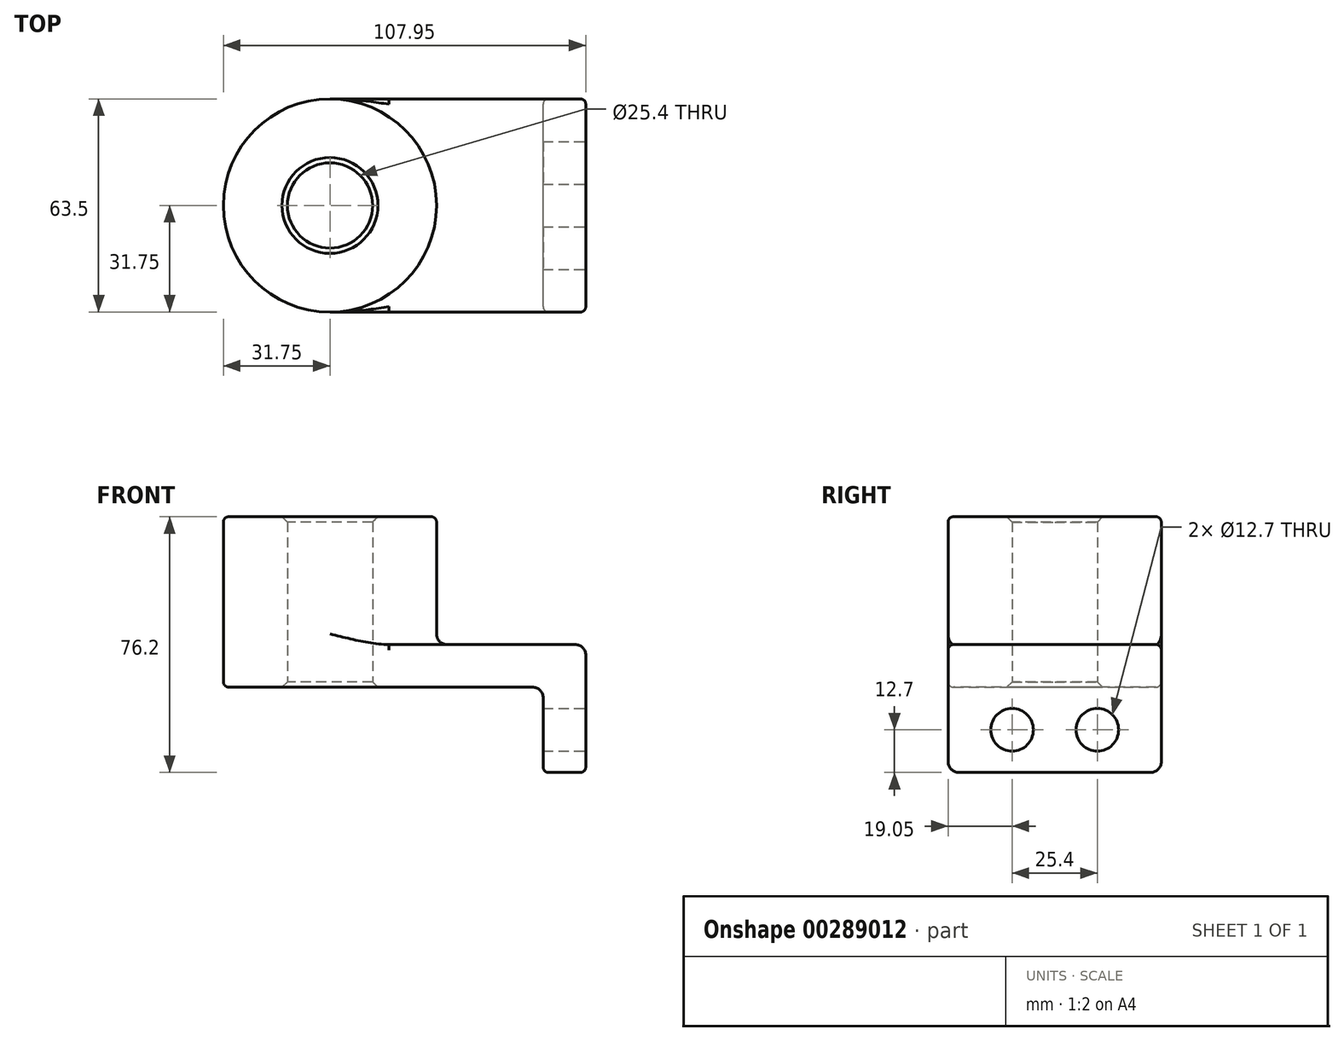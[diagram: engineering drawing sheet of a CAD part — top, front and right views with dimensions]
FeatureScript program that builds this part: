
annotation { "Feature Type Name" : "Feature", "Feature Type Description" : "" }
export const myFeature = defineFeature(function(context is Context, id is Id, definition is map)
    precondition{}
    {
        {
            var Q0;
            Q0=qCreatedBy(makeId("Top.planeOp"),FACE);
            var sketch = newSketch(context, id + "F0", { "sketchPlane" : qUnion([Q0])});
            skLineSegment(sketch, "E0.rect.bottom", {"start": v(-38.1, -31.75) * mm, "end": v(38.1, -31.75) * mm});
            skLineSegment(sketch, "E0.rect.top", {"start": v(-38.1, 31.75) * mm, "end": v(38.1, 31.75) * mm});
            skLineSegment(sketch, "E0.rect.left", {"start": v(-38.1, -31.75) * mm, "end": v(-38.1, 31.75) * mm});
            skLineSegment(sketch, "E0.rect.right", {"start": v(38.1, -31.75) * mm, "end": v(38.1, 31.75) * mm});
            skPoint(sketch, "E0.rect.middle", {"position": v(0, 0) * mm});
            skCircle(sketch, "E1", {"center": v(-38.1, 0) * mm, "radius": 31.75 * mm});
            skCircle(sketch, "E2", {"center": v(-38.1, 0) * mm, "radius": 12.7 * mm});
            skSolve(sketch);
        }
        {
            var Q0;
            {var subQ2=sQuery(id+"F0.wireOp",EDGE,"E0.rect.left");var subQ4=sQuery(id+"F0.wireOp",EDGE,"E0.rect.bottom");var subQ7=sQuery(id+"F0.wireOp",EDGE,"E2");var subQ9=makeQuery(id+"F0.imprint","INTERSECT",VERTEX,{"disambiguationData":[OD(0.0)],"derivedFrom":[subQ2,subQ7]});Q0=qUnion([makeQuery(id+"F0.imprint","IMPRINT",FACE,{"disambiguationData":[TD([[makeQuery(id+"F0.imprint","IMPRINT",EDGE,{"derivedFrom":subQ4}),1.0]])]}),makeQuery(id+"F0.imprint","IMPRINT",FACE,{"disambiguationData":[TD([[makeQuery(id+"F0.imprint","IMPRINT",EDGE,{"disambiguationData":[TD([[subQ9,1.0]])],"derivedFrom":subQ7}),-1.0]])]}),makeQuery(id+"F0.imprint","IMPRINT",FACE,{"disambiguationData":[TD([[makeQuery(id+"F0.imprint","IMPRINT",EDGE,{"disambiguationData":[TD([[subQ9,-1.0]])],"derivedFrom":subQ7}),-1.0]])]})]);}
            extrude(context, id + "F1", {"entities" : qUnion([Q0]), "depth" : 12.7 * mm});
        }
        {
            var Q0;
            {var subQ0=sQuery(id+"F0.wireOp",EDGE,"E2");var subQ1=sQuery(id+"F0.wireOp",EDGE,"E0.rect.left");var subQ3=makeQuery(id+"F0.imprint","INTERSECT",VERTEX,{"disambiguationData":[OD(0.0)],"derivedFrom":[subQ1,subQ0]});Q0=makeQuery(id+"F0.imprint","IMPRINT",FACE,{"disambiguationData":[TD([[makeQuery(id+"F0.imprint","IMPRINT",EDGE,{"disambiguationData":[TD([[subQ3,1.0]])],"derivedFrom":subQ0}),-1.0]])]});}
            var Q1;
            {var subQ0=sQuery(id+"F0.wireOp",EDGE,"E2");var subQ1=sQuery(id+"F0.wireOp",EDGE,"E0.rect.left");var subQ3=makeQuery(id+"F0.imprint","INTERSECT",VERTEX,{"disambiguationData":[OD(0.0)],"derivedFrom":[subQ1,subQ0]});Q1=makeQuery(id+"F0.imprint","IMPRINT",FACE,{"disambiguationData":[TD([[makeQuery(id+"F0.imprint","IMPRINT",EDGE,{"disambiguationData":[TD([[subQ3,-1.0]])],"derivedFrom":subQ0}),-1.0]])]});}
            extrude(context, id + "F2", {"entities" : qUnion([Q0, Q1]), "operationType" : NewBodyOperationType.ADD, "depth" : 50.8 * mm});
        }
        {
            var Q0;
            Q0=makeQuery(id+"F1.opExtrude","SWEPT_FACE",FACE,{"disambiguationData":[OSD([sQuery(id+"F0.wireOp",EDGE,"E0.rect.right")])]});
            var sketch = newSketch(context, id + "F3", { "sketchPlane" : qUnion([Q0])});
            skLineSegment(sketch, "E3.bottom", {"start": v(-31.75, 12.7) * mm, "end": v(31.75, 12.7) * mm});
            skLineSegment(sketch, "E3.top", {"start": v(-31.75, -25.4) * mm, "end": v(31.75, -25.4) * mm});
            skLineSegment(sketch, "E3.left", {"start": v(-31.75, 12.7) * mm, "end": v(-31.75, -25.4) * mm});
            skLineSegment(sketch, "E3.right", {"start": v(31.75, 12.7) * mm, "end": v(31.75, -25.4) * mm});
            skLineSegment(sketch, "E4", {"start": v(0, 0) * mm, "end": v(0, -25.4) * mm, "construction": true});
            skCircle(sketch, "E5", {"center": v(-12.7, -12.7) * mm, "radius": 6.35 * mm});
            skCircle(sketch, "E6.0.MirrorC", {"center": v(12.7, -12.7) * mm, "radius": 6.35 * mm});
            skSolve(sketch);
        }
        {
            var Q0;
            {var subQ3=sQuery(id+"F3.wireOp",EDGE,"E3.bottom");var subQ7=sQuery(id+"F3.wireOp",EDGE,"E3.top");Q0=qUnion([makeQuery(id+"F3.imprint","IMPRINT",FACE,{"disambiguationData":[TD([[makeQuery(id+"F3.imprint","IMPRINT",EDGE,{"derivedFrom":subQ3}),-1.0]])]}),makeQuery(id+"F3.imprint","IMPRINT",FACE,{"disambiguationData":[TD([[makeQuery(id+"F3.imprint","IMPRINT",EDGE,{"derivedFrom":subQ7}),1.0]])]})]);}
            extrude(context, id + "F4", {"entities" : qUnion([Q0]), "operationType" : NewBodyOperationType.ADD, "oppositeDirection" : true, "depth" : 12.7 * mm});
        }
        {
            var Q0;
            {var subQ0=sQuery(id+"F0.wireOp",EDGE,"E1");Q0=makeQuery(id+"F2.boolean.opBoolean","INTERSECT",EDGE,{"derivedFrom":[makeQuery(id+"F1.opExtrude","CAP_FACE",FACE,{"disambiguationData":[OSD([sQuery(id+"F0.wireOp",EDGE,"E0.rect.bottom"),sQuery(id+"F0.wireOp",EDGE,"E0.rect.top"),sQuery(id+"F0.wireOp",EDGE,"E0.rect.right"),subQ0,sQuery(id+"F0.wireOp",EDGE,"E2")])],"isStart":false}),makeQuery(id+"F2.opExtrude","SWEPT_FACE",FACE,{"disambiguationData":[OSD([subQ0])]})]});}
            var Q1;
            Q1=makeQuery(id+"F1.opExtrude","CAP_EDGE",EDGE,{"disambiguationData":[OSD([sQuery(id+"F0.wireOp",EDGE,"E0.rect.right")])],"isStart":false});
            var Q2;
            Q2=makeQuery(id+"F4.opExtrude","SWEPT_EDGE",EDGE,{"disambiguationData":[OSD([sQuery(id+"F3.wireOp",EDGE,"E3.top"),sQuery(id+"F3.wireOp",EDGE,"E3.left")])]});
            var Q3;
            Q3=makeQuery(id+"F4.opExtrude","SWEPT_EDGE",EDGE,{"disambiguationData":[OSD([sQuery(id+"F3.wireOp",EDGE,"E3.top"),sQuery(id+"F3.wireOp",EDGE,"E3.right")])]});
            var Q4;
            Q4=makeQuery(id+"F4.boolean.opBoolean","INTERSECT",EDGE,{"derivedFrom":[makeQuery(id+"F1.opExtrude","CAP_FACE",FACE,{"disambiguationData":[OSD([sQuery(id+"F0.wireOp",EDGE,"E0.rect.bottom"),sQuery(id+"F0.wireOp",EDGE,"E0.rect.top"),sQuery(id+"F0.wireOp",EDGE,"E0.rect.right"),sQuery(id+"F0.wireOp",EDGE,"E1"),sQuery(id+"F0.wireOp",EDGE,"E2")])],"isStart":true}),makeQuery(id+"F4.opExtrude","CAP_FACE",FACE,{"disambiguationData":[OSD([sQuery(id+"F3.wireOp",EDGE,"E3.bottom"),sQuery(id+"F3.wireOp",EDGE,"E3.top"),sQuery(id+"F3.wireOp",EDGE,"E3.left"),sQuery(id+"F3.wireOp",EDGE,"E3.right"),sQuery(id+"F3.wireOp",EDGE,"E5"),sQuery(id+"F3.wireOp",EDGE,"E6.0.MirrorC")])],"isStart":false})]});
            fillet(context, id + "F5", {"entities" : qUnion([Q0, Q1, Q2, Q3, Q4]), "radius" : 3.17 * mm, "tangentPropagation" : true, "allowEdgeOverflow" : false});
        }
        {
            var Q0;
            {var subQ0=sQuery(id+"F0.wireOp",EDGE,"E1");Q0=makeQuery(id+"F2.boolean.opBoolean","MERGE",FACE,{"derivedFrom":[makeQuery(id+"F1.opExtrude","SWEPT_FACE",FACE,{"disambiguationData":[OSD([subQ0])]}),makeQuery(id+"F2.opExtrude","SWEPT_FACE",FACE,{"disambiguationData":[OSD([subQ0])]})]});}
            var Q1;
            Q1=makeQuery(id+"F1.opExtrude","CAP_EDGE",EDGE,{"disambiguationData":[OSD([sQuery(id+"F0.wireOp",EDGE,"E0.rect.bottom")])],"isStart":false});
            fillet(context, id + "F6", {"entities" : qUnion([Q0, Q1]), "radius" : 1.59 * mm, "tangentPropagation" : true, "allowEdgeOverflow" : false});
        }
        {
            var Q0;
            {var subQ0=sQuery(id+"F0.wireOp",EDGE,"E2");Q0=makeQuery(id+"F2.boolean.opBoolean","MERGE",FACE,{"derivedFrom":[makeQuery(id+"F1.opExtrude","SWEPT_FACE",FACE,{"disambiguationData":[OSD([subQ0])]}),makeQuery(id+"F2.opExtrude","SWEPT_FACE",FACE,{"disambiguationData":[OSD([subQ0])]})]});}
            chamfer(context, id + "F7", {"entities" : qUnion([Q0]), "width" : 1.59 * mm, "tangentPropagation" : true});
        }
    });
